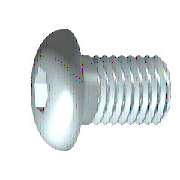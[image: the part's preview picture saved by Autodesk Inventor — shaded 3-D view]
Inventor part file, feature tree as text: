
AUTODESK INVENTOR PART (.ipt)
format: ipt  version: 2015 (Build 190159000, 159)  size: 194,048 bytes
history: native  units: mm (DEFAULTED — no unit token found)
features: sketch x2, extrude x1, plane x1, fillet x1
ambient origin geometry x7: Origin, YZ Plane, XY Plane, X Axis, Y Axis, Z Axis, Center Point
bodies: Solid1 (feature_tree), Body (feature_tree)
feature tree (5):
  extrude  "Slot"  Depth=1.8542mm
  plane  "Work Plane1"
  fillet  "Fillet2"  Radius=1.8542mm
  sketch  "Sketch1"  dims[d1=11.10976mm d2=1.59014mm d3=1.8542mm]
  sketch  "Sketch2"  dims[d4=1.1176mm d5=60.0deg d6=3.5052mm d7=3.5052mm d8=2.287693mm d9=6.6548mm d10=90.0deg d11=10.0mm d12=0.0mm d13=11.10976mm d14=0.0mm d15=0.486918mm d16=0.486918mm d17=1.6002mm d19=0.0mm d26=12.7mm d27=45.0deg d28=0.0mm d29=0.0mm d30=0.1mm]
